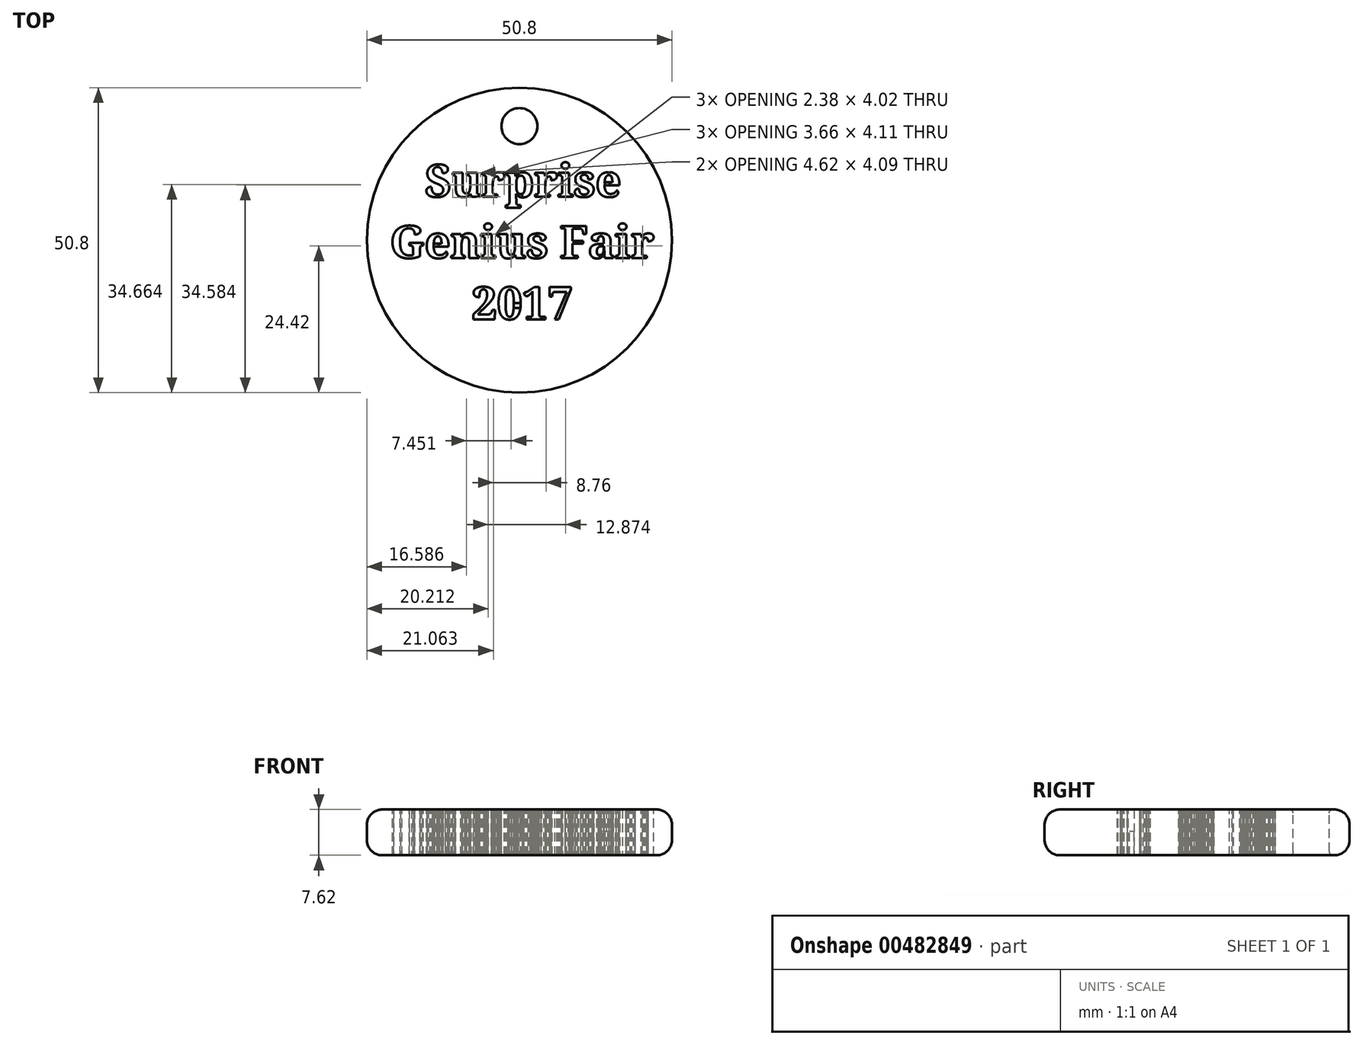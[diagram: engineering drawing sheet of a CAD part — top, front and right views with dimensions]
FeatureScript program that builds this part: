
annotation { "Feature Type Name" : "Feature", "Feature Type Description" : "" }
export const myFeature = defineFeature(function(context is Context, id is Id, definition is map)
    precondition{}
    {
        {
            var Q0;
            Q0=qCreatedBy(makeId("Top.planeOp"),FACE);
            var sketch = newSketch(context, id + "F0", { "sketchPlane" : qUnion([Q0])});
            skCircle(sketch, "E0", {"center": v(0, 0) * mm, "radius": 25.4 * mm});
            skSolve(sketch);
        }
        {
            var Q0;
            Q0=makeQuery(id+"F0.imprint","IMPRINT",FACE,{"disambiguationData":[TD([[makeQuery(id+"F0.imprint","IMPRINT",EDGE,{"derivedFrom":sQuery(id+"F0.wireOp",EDGE,"E0")}),1.0]])]});
            extrude(context, id + "F1", {"entities" : qUnion([Q0]), "depth" : 7.62 * mm});
        }
        {
            var Q0;
            Q0=makeQuery(id+"F1.opExtrude","CAP_EDGE",EDGE,{"disambiguationData":[OSD([sQuery(id+"F0.wireOp",EDGE,"E0")])],"isStart":false});
            var Q1;
            Q1=makeQuery(id+"F1.opExtrude","CAP_EDGE",EDGE,{"disambiguationData":[OSD([sQuery(id+"F0.wireOp",EDGE,"E0")])],"isStart":true});
            fillet(context, id + "F2", {"entities" : qUnion([Q0, Q1]), "radius" : 2.54 * mm, "tangentPropagation" : true, "allowEdgeOverflow" : false});
        }
        {
            var Q0;
            Q0=makeQuery(id+"F1.opExtrude","CAP_FACE",FACE,{"disambiguationData":[OSD([sQuery(id+"F0.wireOp",EDGE,"E0")])],"isStart":false});
            var sketch = newSketch(context, id + "F3", { "sketchPlane" : qUnion([Q0])});
            skText(sketch, "E1", { "text": "   Surprise \nGenius Fair\n       2017", "fontName": "NotoSerif-Bold.ttf"});
            const initialGuessF3  = {"E1": [-0.02156, 0.00721, 1, 0, 0.0054]};
            skSetInitialGuess(sketch, initialGuessF3);
            skSolve(sketch);
        }
        {
            var Q0;
            Q0 = qSketchRegion(id + "F3", true);
            extrude(context, id + "F4", {"entities" : qUnion([Q0]), "operationType" : NewBodyOperationType.REMOVE, "endBound" : BoundingType.THROUGH_ALL, "oppositeDirection" : true, "depth" : 25.4 * mm});
        }
        {
            var Q0;
            Q0=makeQuery(id+"F4.boolean.opBoolean","SPLIT",FACE,{"disambiguationData":[TD([makeQuery(id+"F4.opExtrude","SWEPT_FACE",FACE,{"disambiguationData":[OSD([sQuery(id+"F3.wireOp",EDGE,"E1.sketch_text.stroke-181")])]})])],"derivedFrom":makeQuery(id+"F1.opExtrude","CAP_FACE",FACE,{"disambiguationData":[OSD([sQuery(id+"F0.wireOp",EDGE,"E0")])],"isStart":true})});
            var sketch = newSketch(context, id + "F5", { "sketchPlane" : qUnion([Q0])});
            skLineSegment(sketch, "E2.bottom", {"start": v(0.46, -8.8) * mm, "end": v(-0.34, -8.8) * mm});
            skLineSegment(sketch, "E2.top", {"start": v(0.46, -6.18) * mm, "end": v(-0.34, -6.18) * mm});
            skLineSegment(sketch, "E2.left", {"start": v(0.46, -8.8) * mm, "end": v(0.46, -6.18) * mm});
            skLineSegment(sketch, "E2.right", {"start": v(-0.34, -8.8) * mm, "end": v(-0.34, -6.18) * mm});
            skSolve(sketch);
        }
        {
            var Q0;
            Q0 = qSketchRegion(id + "F5", true);
            extrude(context, id + "F6", {"entities" : qUnion([Q0]), "operationType" : NewBodyOperationType.ADD, "oppositeDirection" : true, "depth" : 3.8 * mm});
        }
        {
            var Q0;
            {var subQ0=sQuery(id+"F0.wireOp",EDGE,"E0");var subQ1=makeQuery(id+"F1.opExtrude","CAP_FACE",FACE,{"disambiguationData":[OSD([subQ0])],"isStart":true});Q0=makeQuery(id+"F6.boolean.opBoolean","MERGE",FACE,{"derivedFrom":[makeQuery(id+"F4.boolean.opBoolean","SPLIT",FACE,{"disambiguationData":[TD([makeQuery(id+"F4.opExtrude","SWEPT_FACE",FACE,{"disambiguationData":[OSD([sQuery(id+"F3.wireOp",EDGE,"E1.sketch_text.stroke-181")])]})])],"derivedFrom":subQ1}),makeQuery(id+"F4.boolean.opBoolean","SPLIT",FACE,{"disambiguationData":[TD([makeQuery(id+"F4.opExtrude","SWEPT_FACE",FACE,{"disambiguationData":[OSD([sQuery(id+"F3.wireOp",EDGE,"E1.sketch_text.stroke-0")])]})])],"derivedFrom":subQ1}),makeQuery(id+"F6.opExtrude","CAP_FACE",FACE,{"disambiguationData":[OSD([sQuery(id+"F5.wireOp",EDGE,"E2.bottom"),sQuery(id+"F5.wireOp",EDGE,"E2.top"),sQuery(id+"F5.wireOp",EDGE,"E2.left"),sQuery(id+"F5.wireOp",EDGE,"E2.right")])],"isStart":true})]});}
            var sketch = newSketch(context, id + "F7", { "sketchPlane" : qUnion([Q0])});
            skLineSegment(sketch, "E3.bottom", {"start": v(14.24, -9.62) * mm, "end": v(15.04, -9.62) * mm});
            skLineSegment(sketch, "E3.top", {"start": v(14.24, -9.14) * mm, "end": v(15.04, -9.14) * mm});
            skLineSegment(sketch, "E3.left", {"start": v(14.24, -9.62) * mm, "end": v(14.24, -9.14) * mm});
            skLineSegment(sketch, "E3.right", {"start": v(15.04, -9.62) * mm, "end": v(15.04, -9.14) * mm});
            skSolve(sketch);
        }
        {
            var Q0;
            Q0=makeQuery(id+"F7.imprint","IMPRINT",FACE,{"disambiguationData":[TD([[makeQuery(id+"F7.imprint","IMPRINT",EDGE,{"derivedFrom":sQuery(id+"F7.wireOp",EDGE,"E3.bottom")}),1.0]])]});
            extrude(context, id + "F8", {"entities" : qUnion([Q0]), "operationType" : NewBodyOperationType.ADD, "oppositeDirection" : true, "depth" : 4 * mm});
        }
        {
            var Q0;
            {var subQ0=sQuery(id+"F0.wireOp",EDGE,"E0");var subQ1=makeQuery(id+"F1.opExtrude","CAP_FACE",FACE,{"disambiguationData":[OSD([subQ0])],"isStart":true});Q0=makeQuery(id+"F8.boolean.opBoolean","MERGE",FACE,{"derivedFrom":[makeQuery(id+"F4.boolean.opBoolean","SPLIT",FACE,{"disambiguationData":[TD([makeQuery(id+"F4.opExtrude","SWEPT_FACE",FACE,{"disambiguationData":[OSD([sQuery(id+"F3.wireOp",EDGE,"E1.sketch_text.stroke-325")])]})])],"derivedFrom":subQ1}),makeQuery(id+"F6.boolean.opBoolean","MERGE",FACE,{"derivedFrom":[makeQuery(id+"F4.boolean.opBoolean","SPLIT",FACE,{"disambiguationData":[TD([makeQuery(id+"F4.opExtrude","SWEPT_FACE",FACE,{"disambiguationData":[OSD([sQuery(id+"F3.wireOp",EDGE,"E1.sketch_text.stroke-181")])]})])],"derivedFrom":subQ1}),makeQuery(id+"F4.boolean.opBoolean","SPLIT",FACE,{"disambiguationData":[TD([makeQuery(id+"F4.opExtrude","SWEPT_FACE",FACE,{"disambiguationData":[OSD([sQuery(id+"F3.wireOp",EDGE,"E1.sketch_text.stroke-0")])]})])],"derivedFrom":subQ1}),makeQuery(id+"F6.opExtrude","CAP_FACE",FACE,{"disambiguationData":[OSD([sQuery(id+"F5.wireOp",EDGE,"E2.bottom"),sQuery(id+"F5.wireOp",EDGE,"E2.top"),sQuery(id+"F5.wireOp",EDGE,"E2.left"),sQuery(id+"F5.wireOp",EDGE,"E2.right")])],"isStart":true})]}),makeQuery(id+"F8.opExtrude","CAP_FACE",FACE,{"disambiguationData":[OSD([sQuery(id+"F7.wireOp",EDGE,"E3.bottom"),sQuery(id+"F7.wireOp",EDGE,"E3.top"),sQuery(id+"F7.wireOp",EDGE,"E3.left"),sQuery(id+"F7.wireOp",EDGE,"E3.right")])],"isStart":true})]});}
            var sketch = newSketch(context, id + "F9", { "sketchPlane" : qUnion([Q0])});
            skLineSegment(sketch, "E4.bottom", {"start": v(-13.45, 0.6) * mm, "end": v(-14.25, 0.6) * mm});
            skLineSegment(sketch, "E4.top", {"start": v(-13.45, 1.32) * mm, "end": v(-14.25, 1.32) * mm});
            skLineSegment(sketch, "E4.left", {"start": v(-13.45, 0.6) * mm, "end": v(-13.45, 1.32) * mm});
            skLineSegment(sketch, "E4.right", {"start": v(-14.25, 0.6) * mm, "end": v(-14.25, 1.32) * mm});
            skSolve(sketch);
        }
        {
            var Q0;
            {var subQ0=sQuery(id+"F9.wireOp",EDGE,"E4.bottom");Q0=makeQuery(id+"F9.imprint","IMPRINT",FACE,{"disambiguationData":[TD([[makeQuery(id+"F9.imprint","IMPRINT",EDGE,{"derivedFrom":subQ0}),-1.0]])]});}
            var Q1;
            {var subQ0=sQuery(id+"F9.wireOp",EDGE,"E4.top");Q1=makeQuery(id+"F9.imprint","IMPRINT",FACE,{"disambiguationData":[TD([[makeQuery(id+"F9.imprint","IMPRINT",EDGE,{"derivedFrom":subQ0}),1.0]])]});}
            extrude(context, id + "F10", {"entities" : qUnion([Q0, Q1]), "operationType" : NewBodyOperationType.ADD, "oppositeDirection" : true, "depth" : 4 * mm});
        }
        {
            var Q0;
            {var subQ0=sQuery(id+"F0.wireOp",EDGE,"E0");var subQ1=makeQuery(id+"F1.opExtrude","CAP_FACE",FACE,{"disambiguationData":[OSD([subQ0])],"isStart":true});Q0=makeQuery(id+"F10.boolean.opBoolean","MERGE",FACE,{"derivedFrom":[makeQuery(id+"F4.boolean.opBoolean","SPLIT",FACE,{"disambiguationData":[TD([makeQuery(id+"F4.opExtrude","SWEPT_FACE",FACE,{"disambiguationData":[OSD([sQuery(id+"F3.wireOp",EDGE,"E1.sketch_text.stroke-404")])]})])],"derivedFrom":subQ1}),makeQuery(id+"F8.boolean.opBoolean","MERGE",FACE,{"derivedFrom":[makeQuery(id+"F4.boolean.opBoolean","SPLIT",FACE,{"disambiguationData":[TD([makeQuery(id+"F4.opExtrude","SWEPT_FACE",FACE,{"disambiguationData":[OSD([sQuery(id+"F3.wireOp",EDGE,"E1.sketch_text.stroke-325")])]})])],"derivedFrom":subQ1}),makeQuery(id+"F6.boolean.opBoolean","MERGE",FACE,{"derivedFrom":[makeQuery(id+"F4.boolean.opBoolean","SPLIT",FACE,{"disambiguationData":[TD([makeQuery(id+"F4.opExtrude","SWEPT_FACE",FACE,{"disambiguationData":[OSD([sQuery(id+"F3.wireOp",EDGE,"E1.sketch_text.stroke-181")])]})])],"derivedFrom":subQ1}),makeQuery(id+"F4.boolean.opBoolean","SPLIT",FACE,{"disambiguationData":[TD([makeQuery(id+"F4.opExtrude","SWEPT_FACE",FACE,{"disambiguationData":[OSD([sQuery(id+"F3.wireOp",EDGE,"E1.sketch_text.stroke-0")])]})])],"derivedFrom":subQ1}),makeQuery(id+"F6.opExtrude","CAP_FACE",FACE,{"disambiguationData":[OSD([sQuery(id+"F5.wireOp",EDGE,"E2.bottom"),sQuery(id+"F5.wireOp",EDGE,"E2.top"),sQuery(id+"F5.wireOp",EDGE,"E2.left"),sQuery(id+"F5.wireOp",EDGE,"E2.right")])],"isStart":true})]}),makeQuery(id+"F8.opExtrude","CAP_FACE",FACE,{"disambiguationData":[OSD([sQuery(id+"F7.wireOp",EDGE,"E3.bottom"),sQuery(id+"F7.wireOp",EDGE,"E3.top"),sQuery(id+"F7.wireOp",EDGE,"E3.left"),sQuery(id+"F7.wireOp",EDGE,"E3.right")])],"isStart":true})]}),makeQuery(id+"F10.opExtrude","CAP_FACE",FACE,{"disambiguationData":[OSD([sQuery(id+"F9.wireOp",EDGE,"E4.bottom"),sQuery(id+"F9.wireOp",EDGE,"E4.top"),sQuery(id+"F9.wireOp",EDGE,"E4.left"),sQuery(id+"F9.wireOp",EDGE,"E4.right")])],"isStart":true})]});}
            var sketch = newSketch(context, id + "F11", { "sketchPlane" : qUnion([Q0])});
            skLineSegment(sketch, "E5.bottom", {"start": v(0.76, 10.49) * mm, "end": v(-1.62, 10.49) * mm});
            skLineSegment(sketch, "E5.top", {"start": v(0.76, 11.29) * mm, "end": v(-1.62, 11.29) * mm});
            skLineSegment(sketch, "E5.left", {"start": v(0.76, 10.49) * mm, "end": v(0.76, 11.29) * mm});
            skLineSegment(sketch, "E5.right", {"start": v(-1.62, 10.49) * mm, "end": v(-1.62, 11.29) * mm});
            skSolve(sketch);
        }
        {
            var Q0;
            Q0 = qSketchRegion(id + "F11", true);
            extrude(context, id + "F12", {"entities" : qUnion([Q0]), "operationType" : NewBodyOperationType.ADD, "oppositeDirection" : true, "depth" : 4 * mm});
        }
        {
            var Q0;
            {var subQ0=sQuery(id+"F0.wireOp",EDGE,"E0");var subQ1=makeQuery(id+"F1.opExtrude","CAP_FACE",FACE,{"disambiguationData":[OSD([subQ0])],"isStart":true});Q0=makeQuery(id+"F12.boolean.opBoolean","MERGE",FACE,{"derivedFrom":[makeQuery(id+"F4.boolean.opBoolean","SPLIT",FACE,{"disambiguationData":[TD([makeQuery(id+"F4.opExtrude","SWEPT_FACE",FACE,{"disambiguationData":[OSD([sQuery(id+"F3.wireOp",EDGE,"E1.sketch_text.stroke-834")])]})])],"derivedFrom":subQ1}),makeQuery(id+"F10.boolean.opBoolean","MERGE",FACE,{"derivedFrom":[makeQuery(id+"F4.boolean.opBoolean","SPLIT",FACE,{"disambiguationData":[TD([makeQuery(id+"F4.opExtrude","SWEPT_FACE",FACE,{"disambiguationData":[OSD([sQuery(id+"F3.wireOp",EDGE,"E1.sketch_text.stroke-404")])]})])],"derivedFrom":subQ1}),makeQuery(id+"F8.boolean.opBoolean","MERGE",FACE,{"derivedFrom":[makeQuery(id+"F4.boolean.opBoolean","SPLIT",FACE,{"disambiguationData":[TD([makeQuery(id+"F4.opExtrude","SWEPT_FACE",FACE,{"disambiguationData":[OSD([sQuery(id+"F3.wireOp",EDGE,"E1.sketch_text.stroke-325")])]})])],"derivedFrom":subQ1}),makeQuery(id+"F6.boolean.opBoolean","MERGE",FACE,{"derivedFrom":[makeQuery(id+"F4.boolean.opBoolean","SPLIT",FACE,{"disambiguationData":[TD([makeQuery(id+"F4.opExtrude","SWEPT_FACE",FACE,{"disambiguationData":[OSD([sQuery(id+"F3.wireOp",EDGE,"E1.sketch_text.stroke-181")])]})])],"derivedFrom":subQ1}),makeQuery(id+"F4.boolean.opBoolean","SPLIT",FACE,{"disambiguationData":[TD([makeQuery(id+"F4.opExtrude","SWEPT_FACE",FACE,{"disambiguationData":[OSD([sQuery(id+"F3.wireOp",EDGE,"E1.sketch_text.stroke-0")])]})])],"derivedFrom":subQ1}),makeQuery(id+"F6.opExtrude","CAP_FACE",FACE,{"disambiguationData":[OSD([sQuery(id+"F5.wireOp",EDGE,"E2.bottom"),sQuery(id+"F5.wireOp",EDGE,"E2.top"),sQuery(id+"F5.wireOp",EDGE,"E2.left"),sQuery(id+"F5.wireOp",EDGE,"E2.right")])],"isStart":true})]}),makeQuery(id+"F8.opExtrude","CAP_FACE",FACE,{"disambiguationData":[OSD([sQuery(id+"F7.wireOp",EDGE,"E3.bottom"),sQuery(id+"F7.wireOp",EDGE,"E3.top"),sQuery(id+"F7.wireOp",EDGE,"E3.left"),sQuery(id+"F7.wireOp",EDGE,"E3.right")])],"isStart":true})]}),makeQuery(id+"F10.opExtrude","CAP_FACE",FACE,{"disambiguationData":[OSD([sQuery(id+"F9.wireOp",EDGE,"E4.bottom"),sQuery(id+"F9.wireOp",EDGE,"E4.top"),sQuery(id+"F9.wireOp",EDGE,"E4.left"),sQuery(id+"F9.wireOp",EDGE,"E4.right")])],"isStart":true})]}),makeQuery(id+"F12.opExtrude","CAP_FACE",FACE,{"disambiguationData":[OSD([sQuery(id+"F11.wireOp",EDGE,"E5.bottom"),sQuery(id+"F11.wireOp",EDGE,"E5.top"),sQuery(id+"F11.wireOp",EDGE,"E5.left"),sQuery(id+"F11.wireOp",EDGE,"E5.right")])],"isStart":true})]});}
            var sketch = newSketch(context, id + "F13", { "sketchPlane" : qUnion([Q0])});
            skLineSegment(sketch, "E6", {"start": v(14.15, 2.48) * mm, "end": v(14.09, 1) * mm});
            skLineSegment(sketch, "E7", {"start": v(14.09, 1) * mm, "end": v(13.31, 1.57) * mm});
            skLineSegment(sketch, "E8", {"start": v(13.31, 1.57) * mm, "end": v(13.39, 3.24) * mm});
            skLineSegment(sketch, "E9", {"start": v(13.39, 3.24) * mm, "end": v(14.15, 2.48) * mm});
            skSolve(sketch);
        }
        {
            var Q0;
            {var subQ1=sQuery(id+"F13.wireOp",EDGE,"E9");Q0=makeQuery(id+"F13.imprint","IMPRINT",FACE,{"disambiguationData":[TD([[makeQuery(id+"F13.imprint","IMPRINT",EDGE,{"derivedFrom":subQ1}),-1.0]])]});}
            var Q1;
            Q1=makeQuery(id+"F13.imprint","IMPRINT",FACE,{"disambiguationData":[TD([[makeQuery(id+"F13.imprint","IMPRINT",EDGE,{"derivedFrom":sQuery(id+"F13.wireOp",EDGE,"E6")}),-1.0]])]});
            extrude(context, id + "F14", {"entities" : qUnion([Q0, Q1]), "operationType" : NewBodyOperationType.ADD, "oppositeDirection" : true, "depth" : 4 * mm});
        }
        {
            var Q0;
            {var subQ0=sQuery(id+"F0.wireOp",EDGE,"E0");Q0=makeQuery(id+"F4.boolean.opBoolean","SPLIT",FACE,{"disambiguationData":[TD([makeQuery(id+"F4.opExtrude","SWEPT_FACE",FACE,{"disambiguationData":[OSD([sQuery(id+"F3.wireOp",EDGE,"E1.sketch_text.stroke-0")])]})])],"derivedFrom":makeQuery(id+"F1.opExtrude","CAP_FACE",FACE,{"disambiguationData":[OSD([subQ0])],"isStart":false})});}
            var sketch = newSketch(context, id + "F15", { "sketchPlane" : qUnion([Q0])});
            skCircle(sketch, "E10", {"center": v(0, 19) * mm, "radius": 3 * mm});
            skSolve(sketch);
        }
        {
            var Q0;
            Q0 = qSketchRegion(id + "F15", true);
            extrude(context, id + "F16", {"entities" : qUnion([Q0]), "operationType" : NewBodyOperationType.REMOVE, "endBound" : BoundingType.THROUGH_ALL, "oppositeDirection" : true, "depth" : 25 * mm});
        }
        {
            var Q0;
            {var subQ0=sQuery(id+"F0.wireOp",EDGE,"E0");Q0=makeQuery(id+"F2.opFillet","BLEND_FACE",FACE,{"disambiguationData":[OSD([subQ0]),TDD([makeQuery(id+"F1.opExtrude","CAP_EDGE",EDGE,{"disambiguationData":[OSD([subQ0])],"isStart":true})])]});}
            var Q1;
            Q1=makeQuery(id+"F16.boolean.opBoolean","COPY",EDGE,{"derivedFrom":makeQuery(id+"F16.opExtrude","CAP_EDGE",EDGE,{"disambiguationData":[OSD([sQuery(id+"F15.wireOp",EDGE,"E10")])],"isStart":true})});
            var Q2;
            Q2=makeQuery(id+"F16.boolean.opBoolean","COPY",FACE,{"derivedFrom":makeQuery(id+"F16.opExtrude","SWEPT_FACE",FACE,{"disambiguationData":[OSD([sQuery(id+"F15.wireOp",EDGE,"E10")])]})});
            fillet(context, id + "F17", {"entities" : qUnion([Q0, Q1, Q2]), "radius" : .6 * mm, "tangentPropagation" : true, "allowEdgeOverflow" : false});
        }
    });
